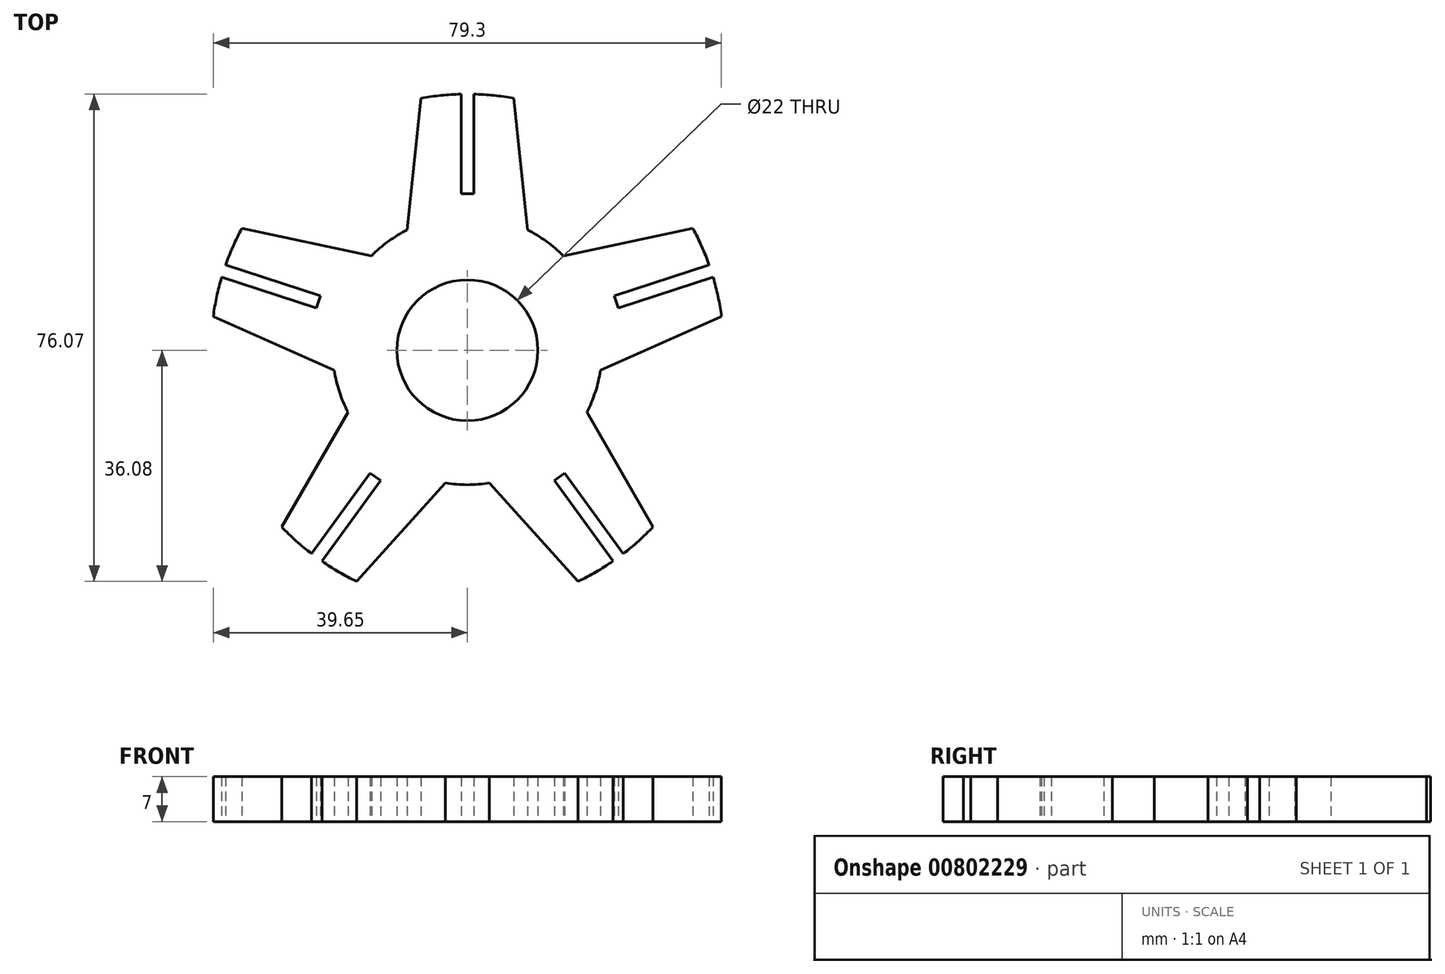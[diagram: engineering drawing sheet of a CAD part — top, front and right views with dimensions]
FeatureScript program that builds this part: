
annotation { "Feature Type Name" : "Feature", "Feature Type Description" : "" }
export const myFeature = defineFeature(function(context is Context, id is Id, definition is map)
    precondition{}
    {
        {
            var Q0;
            Q0=qCreatedBy(makeId("Top.planeOp"),FACE);
            var sketch = newSketch(context, id + "F0", { "sketchPlane" : qUnion([Q0])});
            skArc(sketch, "E0", {"start": v(-0.99, 39.99) * mm, "mid": v(-4.12, 39.79) * mm, "end": v(-7.23, 39.34) * mm});
            skCircle(sketch, "E1", {"center": v(0, 0) * mm, "radius": 11 * mm});
            skCircle(sketch, "E2", {"center": v(0, 0) * mm, "radius": 21 * mm});
            skLineSegment(sketch, "E3", {"start": v(0, 21) * mm, "end": v(0, 39.99) * mm, "construction": true});
            skLineSegment(sketch, "E4.1.0", {"start": v(-19.97, 6.49) * mm, "end": v(-38.04, 12.36) * mm, "construction": true});
            skLineSegment(sketch, "E4.2.0", {"start": v(-12.34, -16.99) * mm, "end": v(-23.51, -32.36) * mm, "construction": true});
            skLineSegment(sketch, "E4.3.0", {"start": v(12.34, -16.99) * mm, "end": v(23.51, -32.36) * mm, "construction": true});
            skLineSegment(sketch, "E4.4.0", {"start": v(19.97, 6.49) * mm, "end": v(38.04, 12.36) * mm, "construction": true});
            skPoint(sketch, "E5", {"position": v(-7.23, 39.34) * mm});
            skPoint(sketch, "E6", {"position": v(-9.4, 18.78) * mm});
            skLineSegment(sketch, "E7", {"start": v(-7.23, 39.34) * mm, "end": v(-9.4, 18.78) * mm});
            skLineSegment(sketch, "E8.1.0", {"start": v(-39.65, 5.29) * mm, "end": v(-20.76, -3.14) * mm});
            skLineSegment(sketch, "E8.2.0", {"start": v(-17.28, -36.08) * mm, "end": v(-3.43, -20.72) * mm});
            skLineSegment(sketch, "E8.3.0", {"start": v(28.97, -27.58) * mm, "end": v(18.64, -9.66) * mm});
            skLineSegment(sketch, "E8.4.0", {"start": v(35.18, 19.03) * mm, "end": v(14.95, 14.75) * mm});
            skLineSegment(sketch, "E9.MirrorCS", {"start": v(7.23, 39.34) * mm, "end": v(9.4, 18.78) * mm});
            skLineSegment(sketch, "E10.1.0", {"start": v(-35.18, 19.03) * mm, "end": v(-14.95, 14.75) * mm});
            skLineSegment(sketch, "E10.2.0", {"start": v(-28.97, -27.58) * mm, "end": v(-18.64, -9.66) * mm});
            skLineSegment(sketch, "E10.3.0", {"start": v(17.28, -36.08) * mm, "end": v(3.43, -20.72) * mm});
            skLineSegment(sketch, "E10.4.0", {"start": v(39.65, 5.29) * mm, "end": v(20.76, -3.14) * mm});
            skLineSegment(sketch, "E11.top", {"start": v(0.99, 24.43) * mm, "end": v(-0.99, 24.43) * mm});
            skLineSegment(sketch, "E11.left", {"start": v(0.99, 39.99) * mm, "end": v(0.99, 24.43) * mm});
            skLineSegment(sketch, "E11.right", {"start": v(-0.99, 39.99) * mm, "end": v(-0.99, 24.43) * mm});
            skPoint(sketch, "E11.middle", {"position": v(0, 32.21) * mm});
            skLineSegment(sketch, "E12.1.0", {"start": v(-37.73, 13.3) * mm, "end": v(-22.93, 8.49) * mm});
            skPoint(sketch, "E12.1.1", {"position": v(-30.63, 9.95) * mm});
            skLineSegment(sketch, "E12.1.3", {"start": v(-38.34, 11.42) * mm, "end": v(-23.54, 6.61) * mm});
            skLineSegment(sketch, "E12.1.5", {"start": v(-22.93, 8.49) * mm, "end": v(-23.54, 6.61) * mm});
            skLineSegment(sketch, "E12.2.0", {"start": v(-24.3, -31.77) * mm, "end": v(-15.16, -19.19) * mm});
            skPoint(sketch, "E12.2.1", {"position": v(-18.93, -26.06) * mm});
            skLineSegment(sketch, "E12.2.3", {"start": v(-22.7, -32.93) * mm, "end": v(-13.56, -20.35) * mm});
            skLineSegment(sketch, "E12.2.5", {"start": v(-15.16, -19.19) * mm, "end": v(-13.56, -20.35) * mm});
            skLineSegment(sketch, "E12.3.0", {"start": v(22.7, -32.93) * mm, "end": v(13.56, -20.35) * mm});
            skPoint(sketch, "E12.3.1", {"position": v(18.93, -26.06) * mm});
            skArc(sketch, "E12.3.2", {"start": v(-35.18, 19.03) * mm, "mid": v(-36.57, 16.21) * mm, "end": v(-37.73, 13.3) * mm});
            skLineSegment(sketch, "E12.3.3", {"start": v(24.3, -31.77) * mm, "end": v(15.16, -19.19) * mm});
            skLineSegment(sketch, "E12.3.5", {"start": v(13.56, -20.35) * mm, "end": v(15.16, -19.19) * mm});
            skLineSegment(sketch, "E12.4.0", {"start": v(38.34, 11.42) * mm, "end": v(23.54, 6.61) * mm});
            skPoint(sketch, "E12.4.1", {"position": v(30.63, 9.95) * mm});
            skLineSegment(sketch, "E12.4.3", {"start": v(37.73, 13.3) * mm, "end": v(22.93, 8.49) * mm});
            skLineSegment(sketch, "E12.4.5", {"start": v(23.54, 6.61) * mm, "end": v(22.93, 8.49) * mm});
            skPoint(sketch, "E13.orphan", {"position": v(0, 40) * mm});
            skArc(sketch, "E14.trimOffspring", {"start": v(7.23, 39.34) * mm, "mid": v(4.12, 39.79) * mm, "end": v(0.99, 39.99) * mm});
            skArc(sketch, "E15.trimOffspring", {"start": v(-28.97, -27.58) * mm, "mid": v(-26.72, -29.77) * mm, "end": v(-24.3, -31.77) * mm});
            skArc(sketch, "E16.trimOffspring", {"start": v(-38.34, 11.42) * mm, "mid": v(-39.11, 8.38) * mm, "end": v(-39.65, 5.29) * mm});
            skArc(sketch, "E17.trimOffspring", {"start": v(17.28, -36.08) * mm, "mid": v(20.05, -34.6) * mm, "end": v(22.7, -32.93) * mm});
            skArc(sketch, "E18.trimOffspring", {"start": v(-22.7, -32.93) * mm, "mid": v(-20.05, -34.6) * mm, "end": v(-17.28, -36.08) * mm});
            skArc(sketch, "E19.trimOffspring", {"start": v(39.65, 5.29) * mm, "mid": v(39.11, 8.38) * mm, "end": v(38.34, 11.42) * mm});
            skArc(sketch, "E20.trimOffspring", {"start": v(24.3, -31.77) * mm, "mid": v(26.72, -29.77) * mm, "end": v(28.97, -27.58) * mm});
            skArc(sketch, "E21.trimOffspring", {"start": v(37.73, 13.3) * mm, "mid": v(36.57, 16.21) * mm, "end": v(35.18, 19.03) * mm});
            skSolve(sketch);
        }
        {
            var Q0;
            Q0=makeQuery(id+"F0.imprint","IMPRINT",FACE,{"disambiguationData":[TD([[makeQuery(id+"F0.imprint","IMPRINT",EDGE,{"derivedFrom":sQuery(id+"F0.wireOp",EDGE,"E1")}),-1.0]])]});
            var Q1;
            {var subQ1=sQuery(id+"F0.wireOp",EDGE,"E7");Q1=makeQuery(id+"F0.imprint","IMPRINT",FACE,{"disambiguationData":[TD([[makeQuery(id+"F0.imprint","IMPRINT",EDGE,{"derivedFrom":subQ1}),1.0]])]});}
            var Q2;
            {var subQ1=sQuery(id+"F0.wireOp",EDGE,"E8.4.0");Q2=makeQuery(id+"F0.imprint","IMPRINT",FACE,{"disambiguationData":[TD([[makeQuery(id+"F0.imprint","IMPRINT",EDGE,{"derivedFrom":subQ1}),1.0]])]});}
            var Q3;
            {var subQ1=sQuery(id+"F0.wireOp",EDGE,"E8.3.0");Q3=makeQuery(id+"F0.imprint","IMPRINT",FACE,{"disambiguationData":[TD([[makeQuery(id+"F0.imprint","IMPRINT",EDGE,{"derivedFrom":subQ1}),1.0]])]});}
            var Q4;
            {var subQ1=sQuery(id+"F0.wireOp",EDGE,"E8.2.0");Q4=makeQuery(id+"F0.imprint","IMPRINT",FACE,{"disambiguationData":[TD([[makeQuery(id+"F0.imprint","IMPRINT",EDGE,{"derivedFrom":subQ1}),1.0]])]});}
            var Q5;
            {var subQ1=sQuery(id+"F0.wireOp",EDGE,"E8.1.0");Q5=makeQuery(id+"F0.imprint","IMPRINT",FACE,{"disambiguationData":[TD([[makeQuery(id+"F0.imprint","IMPRINT",EDGE,{"derivedFrom":subQ1}),1.0]])]});}
            extrude(context, id + "F1", {"entities" : qUnion([Q0, Q1, Q2, Q3, Q4, Q5]), "depth" : 7 * mm, "offsetDistance" : 25 * mm});
        }
    });
